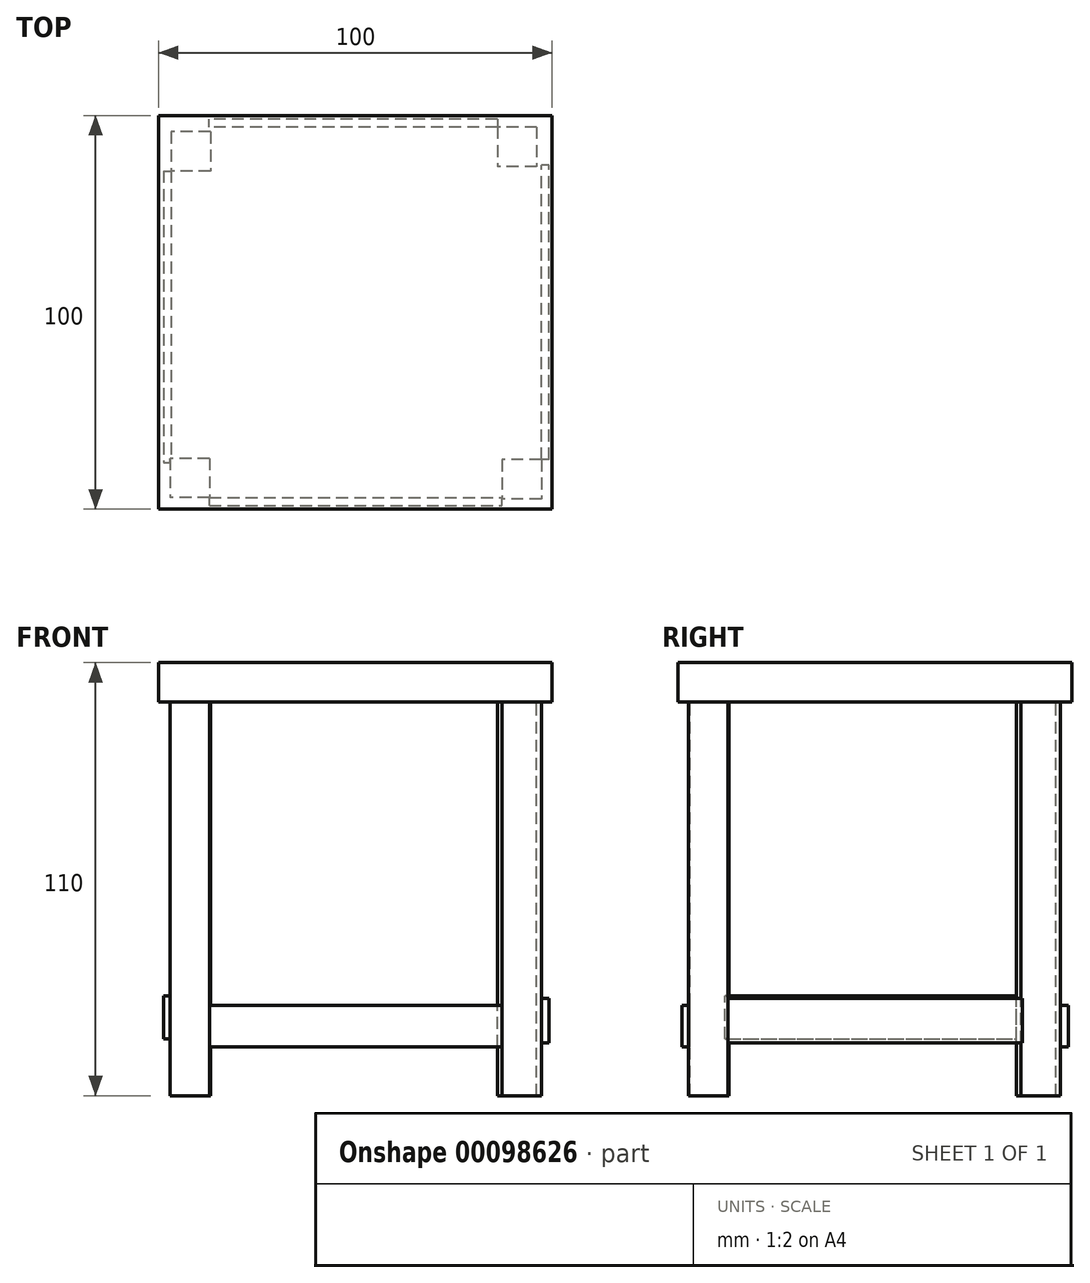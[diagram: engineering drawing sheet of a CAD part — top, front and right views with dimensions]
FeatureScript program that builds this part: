
annotation { "Feature Type Name" : "Feature", "Feature Type Description" : "" }
export const myFeature = defineFeature(function(context is Context, id is Id, definition is map)
    precondition{}
    {
        {
            var Q0;
            Q0=qCreatedBy(makeId("Top.planeOp"),FACE);
            var sketch = newSketch(context, id + "F0", { "sketchPlane" : qUnion([Q0])});
            skLineSegment(sketch, "E0.bottom", {"start": v(-42.82, 57.03) * mm, "end": v(57.18, 57.03) * mm});
            skLineSegment(sketch, "E0.top", {"start": v(-42.82, -42.97) * mm, "end": v(57.18, -42.97) * mm});
            skLineSegment(sketch, "E0.left", {"start": v(-42.82, 57.03) * mm, "end": v(-42.82, -42.97) * mm});
            skLineSegment(sketch, "E0.right", {"start": v(57.18, 57.03) * mm, "end": v(57.18, -42.97) * mm});
            skSolve(sketch);
        }
        {
            var Q0;
            Q0=qCreatedBy(makeId("Top.planeOp"),FACE);
            var sketch = newSketch(context, id + "F1", { "sketchPlane" : qUnion([Q0])});
            skLineSegment(sketch, "E1.bottom", {"start": v(-29.89, -30.03) * mm, "end": v(-39.89, -30.03) * mm});
            skLineSegment(sketch, "E1.top", {"start": v(-29.89, -40.03) * mm, "end": v(-39.89, -40.03) * mm});
            skLineSegment(sketch, "E1.left", {"start": v(-29.89, -30.03) * mm, "end": v(-29.89, -40.03) * mm});
            skLineSegment(sketch, "E1.right", {"start": v(-39.89, -30.03) * mm, "end": v(-39.89, -40.03) * mm});
            skPoint(sketch, "E1.middle", {"position": v(-34.89, -35.03) * mm});
            skSolve(sketch);
        }
        {
            var Q0;
            Q0=makeQuery(id+"F0.imprint","IMPRINT",FACE,{"disambiguationData":[TD([[makeQuery(id+"F0.imprint","IMPRINT",EDGE,{"derivedFrom":sQuery(id+"F0.wireOp",EDGE,"E0.bottom")}),-1.0]])]});
            var sketch = newSketch(context, id + "F2", { "sketchPlane" : qUnion([Q0])});
            skLineSegment(sketch, "E2.bottom", {"start": v(-29.6, 52.95) * mm, "end": v(-39.6, 52.95) * mm});
            skLineSegment(sketch, "E2.top", {"start": v(-29.6, 42.95) * mm, "end": v(-39.6, 42.95) * mm});
            skLineSegment(sketch, "E2.left", {"start": v(-29.6, 52.95) * mm, "end": v(-29.6, 42.95) * mm});
            skLineSegment(sketch, "E2.right", {"start": v(-39.6, 52.95) * mm, "end": v(-39.6, 42.95) * mm});
            skPoint(sketch, "E2.middle", {"position": v(-34.6, 47.95) * mm});
            skSolve(sketch);
        }
        {
            var Q0;
            Q0=makeQuery(id+"F0.imprint","IMPRINT",FACE,{"disambiguationData":[TD([[makeQuery(id+"F0.imprint","IMPRINT",EDGE,{"derivedFrom":sQuery(id+"F0.wireOp",EDGE,"E0.bottom")}),-1.0]])]});
            var sketch = newSketch(context, id + "F3", { "sketchPlane" : qUnion([Q0])});
            skLineSegment(sketch, "E3.bottom", {"start": v(54.4, -30.34) * mm, "end": v(44.4, -30.34) * mm});
            skLineSegment(sketch, "E3.top", {"start": v(54.4, -40.34) * mm, "end": v(44.4, -40.34) * mm});
            skLineSegment(sketch, "E3.left", {"start": v(54.4, -30.34) * mm, "end": v(54.4, -40.34) * mm});
            skLineSegment(sketch, "E3.right", {"start": v(44.4, -30.34) * mm, "end": v(44.4, -40.34) * mm});
            skPoint(sketch, "E3.middle", {"position": v(49.4, -35.34) * mm});
            skSolve(sketch);
        }
        {
            var Q0;
            Q0=makeQuery(id+"F2.imprint","IMPRINT",FACE,{"disambiguationData":[TD([[makeQuery(id+"F2.imprint","IMPRINT",EDGE,{"derivedFrom":sQuery(id+"F2.wireOp",EDGE,"E2.bottom")}),-1.0]])]});
            var sketch = newSketch(context, id + "F4", { "sketchPlane" : qUnion([Q0])});
            skLineSegment(sketch, "E4.bottom", {"start": v(53.22, 54.13) * mm, "end": v(43.22, 54.13) * mm});
            skLineSegment(sketch, "E4.top", {"start": v(53.22, 44.13) * mm, "end": v(43.22, 44.13) * mm});
            skLineSegment(sketch, "E4.left", {"start": v(53.22, 54.13) * mm, "end": v(53.22, 44.13) * mm});
            skLineSegment(sketch, "E4.right", {"start": v(43.22, 54.13) * mm, "end": v(43.22, 44.13) * mm});
            skPoint(sketch, "E4.middle", {"position": v(48.22, 49.13) * mm});
            skSolve(sketch);
        }
        {
            var Q0;
            Q0 = qSketchRegion(id + "F1", true);
            extrude(context, id + "F5", {"entities" : qUnion([Q0]), "oppositeDirection" : true, "depth" : 100 * mm});
        }
        {
            var Q0;
            Q0 = qSketchRegion(id + "F2", true);
            extrude(context, id + "F6", {"entities" : qUnion([Q0]), "oppositeDirection" : true, "depth" : 100 * mm});
        }
        {
            var Q0;
            Q0 = qSketchRegion(id + "F3", true);
            extrude(context, id + "F7", {"entities" : qUnion([Q0]), "oppositeDirection" : true, "depth" : 100 * mm});
        }
        {
            var Q0;
            Q0 = qSketchRegion(id + "F4", true);
            extrude(context, id + "F8", {"entities" : qUnion([Q0]), "oppositeDirection" : true, "depth" : 100 * mm});
        }
        {
            var Q0;
            Q0 = qSketchRegion(id + "F0", true);
            extrude(context, id + "F9", {"entities" : qUnion([Q0]), "depth" : 10 * mm});
        }
        {
            var Q0;
            Q0=makeQuery(id+"F7.opExtrude","SWEPT_FACE",FACE,{"disambiguationData":[OSD([sQuery(id+"F3.wireOp",EDGE,"E3.left")])]});
            var sketch = newSketch(context, id + "F10", { "sketchPlane" : qUnion([Q0])});
            skLineSegment(sketch, "E5", {"start": v(-30.34, -75.29) * mm, "end": v(44.48, -75.29) * mm});
            skLineSegment(sketch, "E6", {"start": v(44.48, -75.29) * mm, "end": v(44.48, -86.58) * mm});
            skLineSegment(sketch, "E7", {"start": v(44.48, -86.58) * mm, "end": v(-30.34, -86.58) * mm});
            skSolve(sketch);
        }
        {
            var Q0;
            {var subQ0=sQuery(id+"F10.wireOp",EDGE,"E5");Q0=makeQuery(id+"F10.imprint","IMPRINT",FACE,{"disambiguationData":[TD([[makeQuery(id+"F10.imprint","IMPRINT",EDGE,{"derivedFrom":subQ0}),-1.0]])]});}
            extrude(context, id + "F11", {"entities" : qUnion([Q0]), "depth" : 2 * mm});
        }
        {
            var Q0;
            Q0=makeQuery(id+"F5.opExtrude","SWEPT_FACE",FACE,{"disambiguationData":[OSD([sQuery(id+"F1.wireOp",EDGE,"E1.top")])]});
            var sketch = newSketch(context, id + "F12", { "sketchPlane" : qUnion([Q0])});
            skLineSegment(sketch, "E8", {"start": v(-29.89, -77) * mm, "end": v(44.48, -77) * mm});
            skLineSegment(sketch, "E9", {"start": v(44.48, -77) * mm, "end": v(44.48, -87.6) * mm});
            skLineSegment(sketch, "E10", {"start": v(-29.89, -77) * mm, "end": v(-29.89, -87.6) * mm});
            skLineSegment(sketch, "E11", {"start": v(-29.89, -87.6) * mm, "end": v(44.48, -87.6) * mm});
            skSolve(sketch);
        }
        {
            var Q0;
            Q0=makeQuery(id+"F12.imprint","IMPRINT",FACE,{"disambiguationData":[TD([[makeQuery(id+"F12.imprint","IMPRINT",EDGE,{"derivedFrom":sQuery(id+"F12.wireOp",EDGE,"E8")}),-1.0]])]});
            extrude(context, id + "F13", {"entities" : qUnion([Q0]), "operationType" : NewBodyOperationType.ADD, "depth" : 2 * mm});
        }
        {
            var Q0;
            Q0=makeQuery(id+"F6.opExtrude","SWEPT_FACE",FACE,{"disambiguationData":[OSD([sQuery(id+"F2.wireOp",EDGE,"E2.right")])]});
            var sketch = newSketch(context, id + "F14", { "sketchPlane" : qUnion([Q0])});
            skLineSegment(sketch, "E12", {"start": v(-42.95, -74.6) * mm, "end": v(31.14, -74.6) * mm});
            skLineSegment(sketch, "E13", {"start": v(31.14, -74.6) * mm, "end": v(31.14, -85.56) * mm});
            skLineSegment(sketch, "E14", {"start": v(31.14, -85.56) * mm, "end": v(-42.95, -85.56) * mm});
            skLineSegment(sketch, "E15", {"start": v(-42.95, -85.56) * mm, "end": v(-42.95, -74.6) * mm});
            skSolve(sketch);
        }
        {
            var Q0;
            Q0=makeQuery(id+"F14.imprint","IMPRINT",FACE,{"disambiguationData":[TD([[makeQuery(id+"F14.imprint","IMPRINT",EDGE,{"derivedFrom":sQuery(id+"F14.wireOp",EDGE,"E12")}),-1.0]])]});
            extrude(context, id + "F15", {"entities" : qUnion([Q0]), "operationType" : NewBodyOperationType.ADD, "depth" : 2 * mm});
        }
        {
            var Q0;
            Q0=makeQuery(id+"F8.opExtrude","SWEPT_FACE",FACE,{"disambiguationData":[OSD([sQuery(id+"F4.wireOp",EDGE,"E4.bottom")])]});
            var sketch = newSketch(context, id + "F16", { "sketchPlane" : qUnion([Q0])});
            skLineSegment(sketch, "E16", {"start": v(-43.22, -77) * mm, "end": v(30.11, -77) * mm});
            skLineSegment(sketch, "E17", {"start": v(30.11, -77) * mm, "end": v(30.11, -87.6) * mm});
            skLineSegment(sketch, "E18", {"start": v(30.11, -87.6) * mm, "end": v(-43.22, -87.6) * mm});
            skLineSegment(sketch, "E19", {"start": v(-43.22, -87.6) * mm, "end": v(-43.22, -77) * mm});
            skSolve(sketch);
        }
        {
            var Q0;
            Q0=makeQuery(id+"F16.imprint","IMPRINT",FACE,{"disambiguationData":[TD([[makeQuery(id+"F16.imprint","IMPRINT",EDGE,{"derivedFrom":sQuery(id+"F16.wireOp",EDGE,"E16")}),-1.0]])]});
            extrude(context, id + "F17", {"entities" : qUnion([Q0]), "depth" : 2 * mm});
        }
    });
